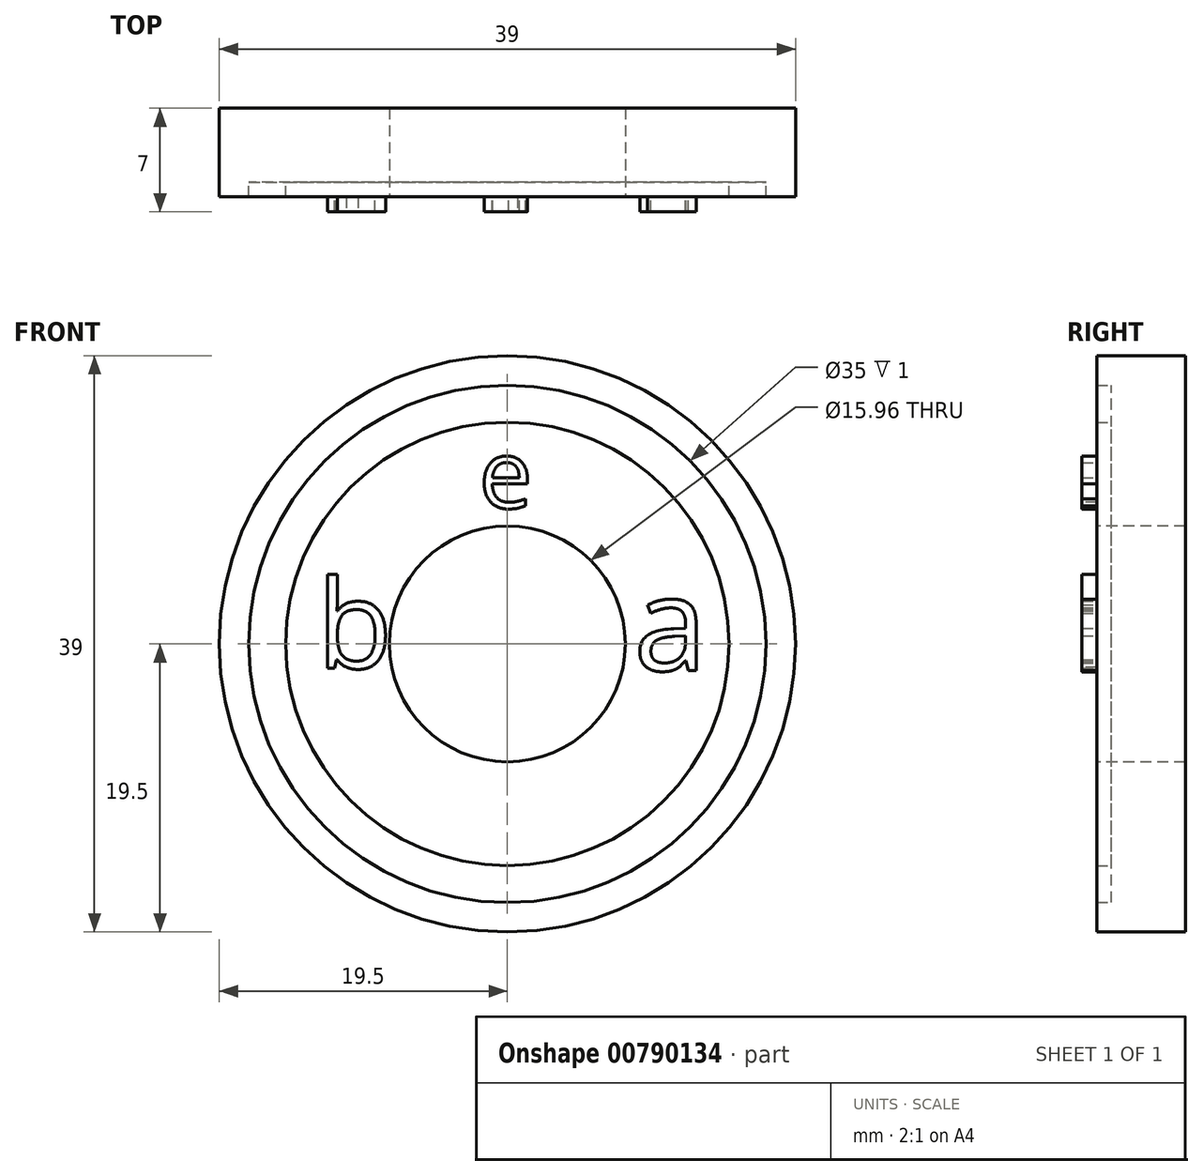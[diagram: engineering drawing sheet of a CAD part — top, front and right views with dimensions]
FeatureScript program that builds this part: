
annotation { "Feature Type Name" : "Feature", "Feature Type Description" : "" }
export const myFeature = defineFeature(function(context is Context, id is Id, definition is map)
    precondition{}
    {
        {
            var Q0;
            Q0=qCreatedBy(makeId("Front.planeOp"),FACE);
            var sketch = newSketch(context, id + "F0", { "sketchPlane" : qUnion([Q0])});
            skCircle(sketch, "E0", {"center": v(0, 0) * mm, "radius": 19.5 * mm});
            skSolve(sketch);
        }
        {
            var Q0;
            Q0 = qSketchRegion(id + "F0", true);
            extrude(context, id + "F1", {"entities" : qUnion([Q0]), "endBound" : BoundingType.SYMMETRIC, "depth" : 5 * mm, "offsetDistance" : 25 * mm});
        }
        {
            var Q0;
            Q0=makeQuery(id+"F1.opExtrude","CAP_FACE",FACE,{"disambiguationData":[OSD([sQuery(id+"F0.wireOp",EDGE,"E0")])],"isStart":false});
            var sketch = newSketch(context, id + "F2", { "sketchPlane" : qUnion([Q0])});
            skCircle(sketch, "E1", {"center": v(0, 0) * mm, "radius": 15 * mm});
            skCircle(sketch, "E2", {"center": v(0, 0) * mm, "radius": 17.5 * mm});
            skSolve(sketch);
        }
        {
            var Q0;
            Q0=makeQuery(id+"F2.imprint","IMPRINT",FACE,{"disambiguationData":[TD([[makeQuery(id+"F2.imprint","IMPRINT",EDGE,{"derivedFrom":sQuery(id+"F2.wireOp",EDGE,"E2")}),-1.0]])]});
            var Q1;
            Q1=makeQuery(id+"F2.imprint","IMPRINT",FACE,{"disambiguationData":[TD([[makeQuery(id+"F2.imprint","IMPRINT",EDGE,{"derivedFrom":sQuery(id+"F2.wireOp",EDGE,"E1")}),1.0]])]});
            extrude(context, id + "F3", {"entities" : qUnion([Q0, Q1]), "operationType" : NewBodyOperationType.ADD, "depth" : 1 * mm, "offsetDistance" : 25 * mm});
        }
        {
            var Q0;
            Q0=makeQuery(id+"F3.opExtrude","CAP_FACE",FACE,{"disambiguationData":[OSD([sQuery(id+"F2.wireOp",EDGE,"E1")])],"isStart":false});
            var sketch = newSketch(context, id + "F4", { "sketchPlane" : qUnion([Q0])});
            skSolve(sketch);
        }
        {
            var Q0;
            Q0=makeQuery(id+"F4.imprint","IMPRINT",FACE,{"disambiguationData":[TD([[makeQuery(id+"F4.imprint","IMPRINT",EDGE,{"derivedFrom":makeQuery(id+"F3.opExtrude","CAP_EDGE",EDGE,{"disambiguationData":[OSD([sQuery(id+"F2.wireOp",EDGE,"E1")])],"isStart":false})}),1.0]])]});
            var sketch = newSketch(context, id + "F5", { "sketchPlane" : qUnion([Q0])});
            skCircle(sketch, "E3", {"center": v(0, 0) * mm, "radius": 7.98 * mm});
            skSolve(sketch);
        }
        {
            var Q0;
            Q0 = qSketchRegion(id + "F5", true);
            extrude(context, id + "F6", {"entities" : qUnion([Q0]), "operationType" : NewBodyOperationType.REMOVE, "endBound" : BoundingType.THROUGH_ALL, "oppositeDirection" : true, "depth" : 25 * mm, "offsetDistance" : 25 * mm});
        }
        {
            var Q0;
            Q0=makeQuery(id+"F4.imprint","IMPRINT",FACE,{"disambiguationData":[TD([[makeQuery(id+"F4.imprint","IMPRINT",EDGE,{"derivedFrom":makeQuery(id+"F3.opExtrude","CAP_EDGE",EDGE,{"disambiguationData":[OSD([sQuery(id+"F2.wireOp",EDGE,"E1")])],"isStart":false})}),1.0]])]});
            var sketch = newSketch(context, id + "F7", { "sketchPlane" : qUnion([Q0])});
            skText(sketch, "E4", { "text": "b\n", "fontName": "OpenSans-Regular.ttf"});
            skText(sketch, "E5", { "text": "e\n\n\n\n\n", "fontName": "OpenSans-Regular.ttf"});
            skText(sketch, "E6", { "text": "a\n", "fontName": "OpenSans-Regular.ttf"});
            const initialGuessF7  = {"E4": [-0.0129, -0.00165, 1, 0, 0.00601], "E5": [-0.00193, 0.00919, 1, 0, 0.00466], "E6": [0.00855, -0.0018, 1, 0, 0.0064]};
            skSetInitialGuess(sketch, initialGuessF7);
            skSolve(sketch);
        }
        {
            var Q0;
            Q0 = qSketchRegion(id + "F7", true);
            extrude(context, id + "F8", {"entities" : qUnion([Q0]), "operationType" : NewBodyOperationType.ADD, "depth" : 1 * mm, "offsetDistance" : 25 * mm});
        }
    });
